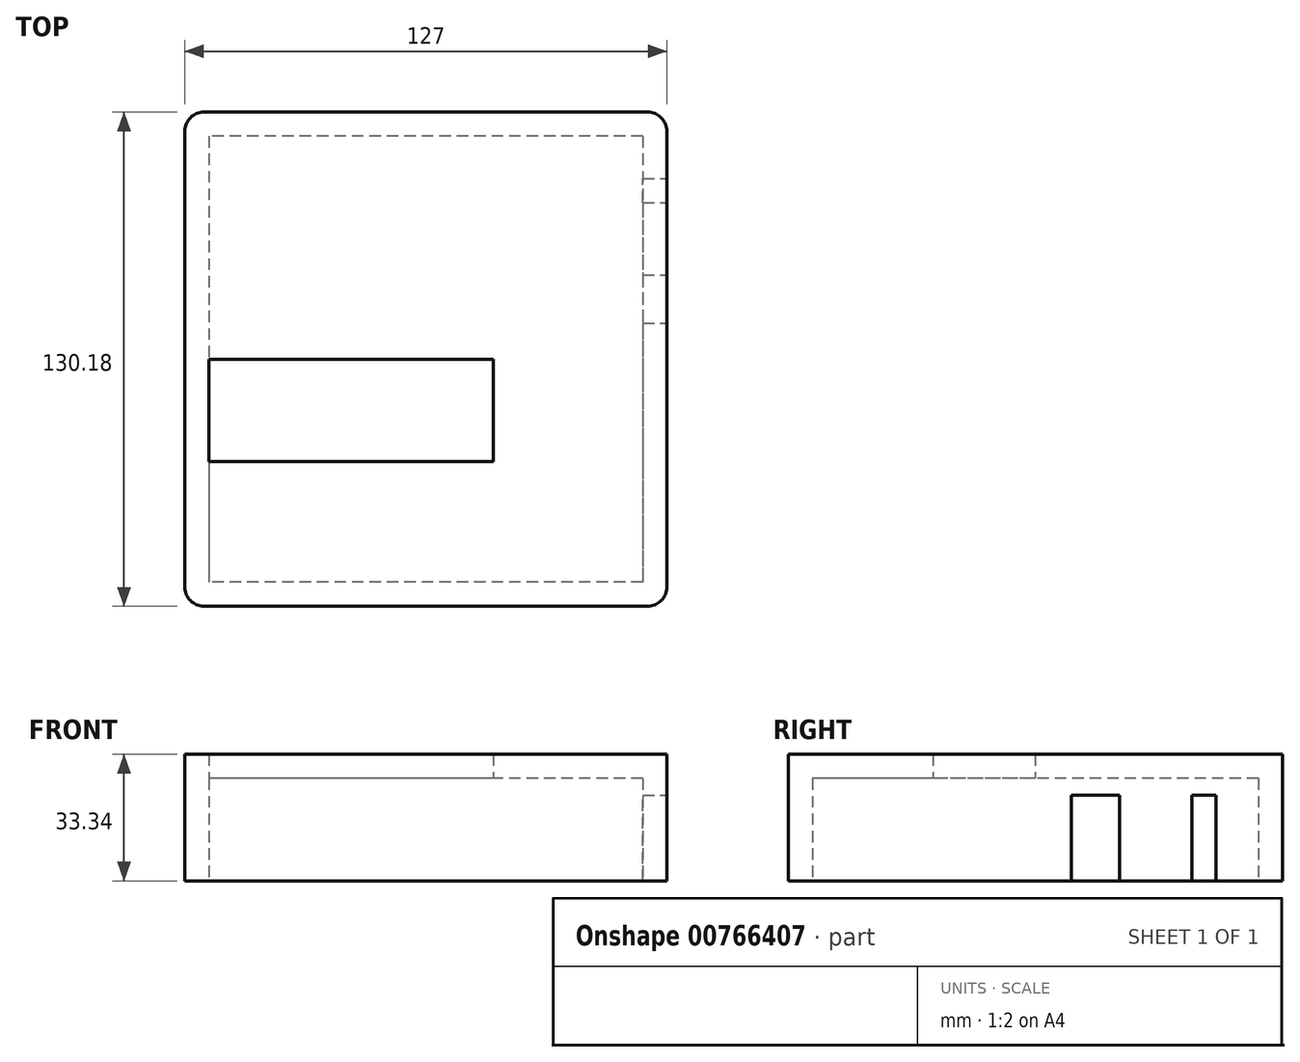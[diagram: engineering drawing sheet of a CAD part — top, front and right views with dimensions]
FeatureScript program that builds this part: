
annotation { "Feature Type Name" : "Feature", "Feature Type Description" : "" }
export const myFeature = defineFeature(function(context is Context, id is Id, definition is map)
    precondition{}
    {
        {
            var Q0;
            Q0=qCreatedBy(makeId("Top.planeOp"),FACE);
            var sketch = newSketch(context, id + "F0", { "sketchPlane" : qUnion([Q0])});
            skLineSegment(sketch, "E0.bottom", {"start": v(0, 0) * mm, "end": v(-127, 0) * mm});
            skLineSegment(sketch, "E0.top", {"start": v(0, -130.18) * mm, "end": v(-127, -130.18) * mm});
            skLineSegment(sketch, "E0.left", {"start": v(0, 0) * mm, "end": v(0, -130.18) * mm});
            skLineSegment(sketch, "E0.right", {"start": v(-127, 0) * mm, "end": v(-127, -130.18) * mm});
            skSolve(sketch);
        }
        {
            var Q0;
            Q0=makeQuery(id+"F0.imprint","IMPRINT",FACE,{"disambiguationData":[TD([[makeQuery(id+"F0.imprint","IMPRINT",EDGE,{"derivedFrom":sQuery(id+"F0.wireOp",EDGE,"E0.bottom")}),1.0]])]});
            extrude(context, id + "F1", {"entities" : qUnion([Q0]), "depth" : 33.34 * mm, "offsetDistance" : 25.4 * mm});
        }
        {
            var Q0;
            Q0=makeQuery(id+"F1.opExtrude","CAP_FACE",FACE,{"disambiguationData":[OSD([sQuery(id+"F0.wireOp",EDGE,"E0.bottom"),sQuery(id+"F0.wireOp",EDGE,"E0.top"),sQuery(id+"F0.wireOp",EDGE,"E0.left"),sQuery(id+"F0.wireOp",EDGE,"E0.right")])],"isStart":true});
            shell(context, id + "F2", {"entities" : qUnion([Q0]), "thickness" : 6.35 * mm});
        }
        {
            var Q0;
            Q0=makeQuery(id+"F1.opExtrude","CAP_FACE",FACE,{"disambiguationData":[OSD([sQuery(id+"F0.wireOp",EDGE,"E0.bottom"),sQuery(id+"F0.wireOp",EDGE,"E0.top"),sQuery(id+"F0.wireOp",EDGE,"E0.left"),sQuery(id+"F0.wireOp",EDGE,"E0.right")])],"isStart":true});
            var sketch = newSketch(context, id + "F3", { "sketchPlane" : qUnion([Q0])});
            skLineSegment(sketch, "E1", {"start": v(-314.03, -9.79) * mm, "end": v(-223.86, -9.79) * mm});
            skLineSegment(sketch, "E2", {"start": v(-314.03, -9.79) * mm, "end": v(-260.06, -9.79) * mm});
            skLineSegment(sketch, "E3", {"start": v(-260.06, -15.82) * mm, "end": v(-260.06, -22.3) * mm});
            skLineSegment(sketch, "E4.bottom", {"start": v(-260.06, -22.3) * mm, "end": v(-223.86, -22.3) * mm});
            skLineSegment(sketch, "E4.top", {"start": v(-260.06, -96.91) * mm, "end": v(-223.86, -96.91) * mm});
            skLineSegment(sketch, "E4.left", {"start": v(-260.06, -22.3) * mm, "end": v(-260.06, -96.91) * mm});
            skLineSegment(sketch, "E4.right", {"start": v(-223.86, -22.3) * mm, "end": v(-223.86, -96.91) * mm});
            skLineSegment(sketch, "E5", {"start": v(-193.07, -15.82) * mm, "end": v(-193.07, -133.93) * mm});
            skLineSegment(sketch, "E6", {"start": v(-120.65, 123.83) * mm, "end": v(-120.65, 92.08) * mm});
            skLineSegment(sketch, "E7", {"start": v(-120.65, 6.35) * mm, "end": v(-120.65, 65.09) * mm});
            skLineSegment(sketch, "E8.bottom", {"start": v(-120.65, 92.08) * mm, "end": v(-45.72, 92.08) * mm});
            skLineSegment(sketch, "E8.top", {"start": v(-120.65, 65.09) * mm, "end": v(-45.72, 65.09) * mm});
            skLineSegment(sketch, "E8.left", {"start": v(-120.65, 92.08) * mm, "end": v(-120.65, 65.09) * mm});
            skLineSegment(sketch, "E8.right", {"start": v(-45.72, 92.08) * mm, "end": v(-45.72, 65.09) * mm});
            skLineSegment(sketch, "E9", {"start": v(-127, 0) * mm, "end": v(0, 0) * mm});
            skLineSegment(sketch, "E10", {"start": v(0, 130.18) * mm, "end": v(0, 0) * mm});
            skLineSegment(sketch, "E11", {"start": v(-6.35, 123.83) * mm, "end": v(-6.35, 6.35) * mm});
            skSolve(sketch);
        }
        {
            var Q0;
            Q0=makeQuery(id+"F3.imprint","IMPRINT",FACE,{"disambiguationData":[TD([[makeQuery(id+"F3.imprint","IMPRINT",EDGE,{"derivedFrom":sQuery(id+"F3.wireOp",EDGE,"E8.bottom")}),-1.0]])]});
            extrude(context, id + "F4", {"entities" : qUnion([Q0]), "operationType" : NewBodyOperationType.REMOVE, "oppositeDirection" : true, "depth" : 35.05 * mm, "offsetDistance" : 25.4 * mm});
        }
        {
            var Q0;
            Q0=makeQuery(id+"F1.opExtrude","SWEPT_FACE",FACE,{"disambiguationData":[OSD([sQuery(id+"F0.wireOp",EDGE,"E0.left")])]});
            var sketch = newSketch(context, id + "F5", { "sketchPlane" : qUnion([Q0])});
            skLineSegment(sketch, "E12", {"start": v(0, 0) * mm, "end": v(-23.81, 0) * mm});
            skLineSegment(sketch, "E13", {"start": v(0, 33.34) * mm, "end": v(-17.46, 33.34) * mm});
            skLineSegment(sketch, "E14", {"start": v(-17.46, -8.65) * mm, "end": v(-17.46, 22.54) * mm});
            skLineSegment(sketch, "E15.bottom", {"start": v(-23.81, -8.65) * mm, "end": v(-17.46, -8.65) * mm});
            skLineSegment(sketch, "E15.top", {"start": v(-23.81, 22.54) * mm, "end": v(-17.46, 22.54) * mm});
            skLineSegment(sketch, "E15.left", {"start": v(-23.81, -8.65) * mm, "end": v(-23.81, 22.54) * mm});
            skLineSegment(sketch, "E16", {"start": v(0, 33.34) * mm, "end": v(-53.98, 33.34) * mm});
            skLineSegment(sketch, "E17.bottom", {"start": v(-42.86, -8.65) * mm, "end": v(-55.56, -8.65) * mm});
            skLineSegment(sketch, "E17.top", {"start": v(-42.86, 22.54) * mm, "end": v(-55.56, 22.54) * mm});
            skLineSegment(sketch, "E17.left", {"start": v(-42.86, -8.65) * mm, "end": v(-42.86, 22.54) * mm});
            skLineSegment(sketch, "E17.right", {"start": v(-55.56, -8.65) * mm, "end": v(-55.56, 22.54) * mm});
            skSolve(sketch);
        }
        {
            var Q0;
            Q0=makeQuery(id+"F5.imprint","IMPRINT",FACE,{"disambiguationData":[TD([[makeQuery(id+"F5.imprint","IMPRINT",EDGE,{"derivedFrom":sQuery(id+"F5.wireOp",EDGE,"E17.bottom")}),-1.0]])]});
            var Q1;
            Q1=makeQuery(id+"F5.imprint","IMPRINT",FACE,{"disambiguationData":[TD([[makeQuery(id+"F5.imprint","IMPRINT",EDGE,{"derivedFrom":sQuery(id+"F5.wireOp",EDGE,"E15.bottom")}),1.0]])]});
            extrude(context, id + "F6", {"entities" : qUnion([Q0, Q1]), "operationType" : NewBodyOperationType.REMOVE, "oppositeDirection" : true, "depth" : 25.4 * mm, "offsetDistance" : 25.4 * mm});
        }
        {
            var Q0;
            Q0=makeQuery(id+"F1.opExtrude","SWEPT_EDGE",EDGE,{"disambiguationData":[OSD([sQuery(id+"F0.wireOp",EDGE,"E0.bottom"),sQuery(id+"F0.wireOp",EDGE,"E0.right")])]});
            var Q1;
            Q1=makeQuery(id+"F1.opExtrude","SWEPT_EDGE",EDGE,{"disambiguationData":[OSD([sQuery(id+"F0.wireOp",EDGE,"E0.top"),sQuery(id+"F0.wireOp",EDGE,"E0.right")])]});
            var Q2;
            Q2=makeQuery(id+"F1.opExtrude","SWEPT_EDGE",EDGE,{"disambiguationData":[OSD([sQuery(id+"F0.wireOp",EDGE,"E0.top"),sQuery(id+"F0.wireOp",EDGE,"E0.left")])]});
            var Q3;
            Q3=makeQuery(id+"F1.opExtrude","SWEPT_EDGE",EDGE,{"disambiguationData":[OSD([sQuery(id+"F0.wireOp",EDGE,"E0.bottom"),sQuery(id+"F0.wireOp",EDGE,"E0.left")])]});
            fillet(context, id + "F7", {"entities" : qUnion([Q0, Q1, Q2, Q3]), "radius" : 5.08 * mm, "tangentPropagation" : true, "allowEdgeOverflow" : false});
        }
        {
            var Q0;
            {var subQ0=sQuery(id+"F5.wireOp",EDGE,"E17.top");Q0=makeQuery(id+"F5.imprint","IMPRINT",FACE,{"disambiguationData":[TD([[makeQuery(id+"F5.imprint","IMPRINT",EDGE,{"derivedFrom":subQ0}),1.0]])]});}
            var Q1;
            {var subQ5=sQuery(id+"F5.wireOp",EDGE,"E15.top");Q1=makeQuery(id+"F5.imprint","IMPRINT",FACE,{"disambiguationData":[TD([[makeQuery(id+"F5.imprint","IMPRINT",EDGE,{"derivedFrom":subQ5}),-1.0]])]});}
            extrude(context, id + "F8", {"entities" : qUnion([Q0, Q1]), "operationType" : NewBodyOperationType.REMOVE, "oppositeDirection" : true, "depth" : 25.4 * mm, "offsetDistance" : 25.4 * mm});
        }
    });
